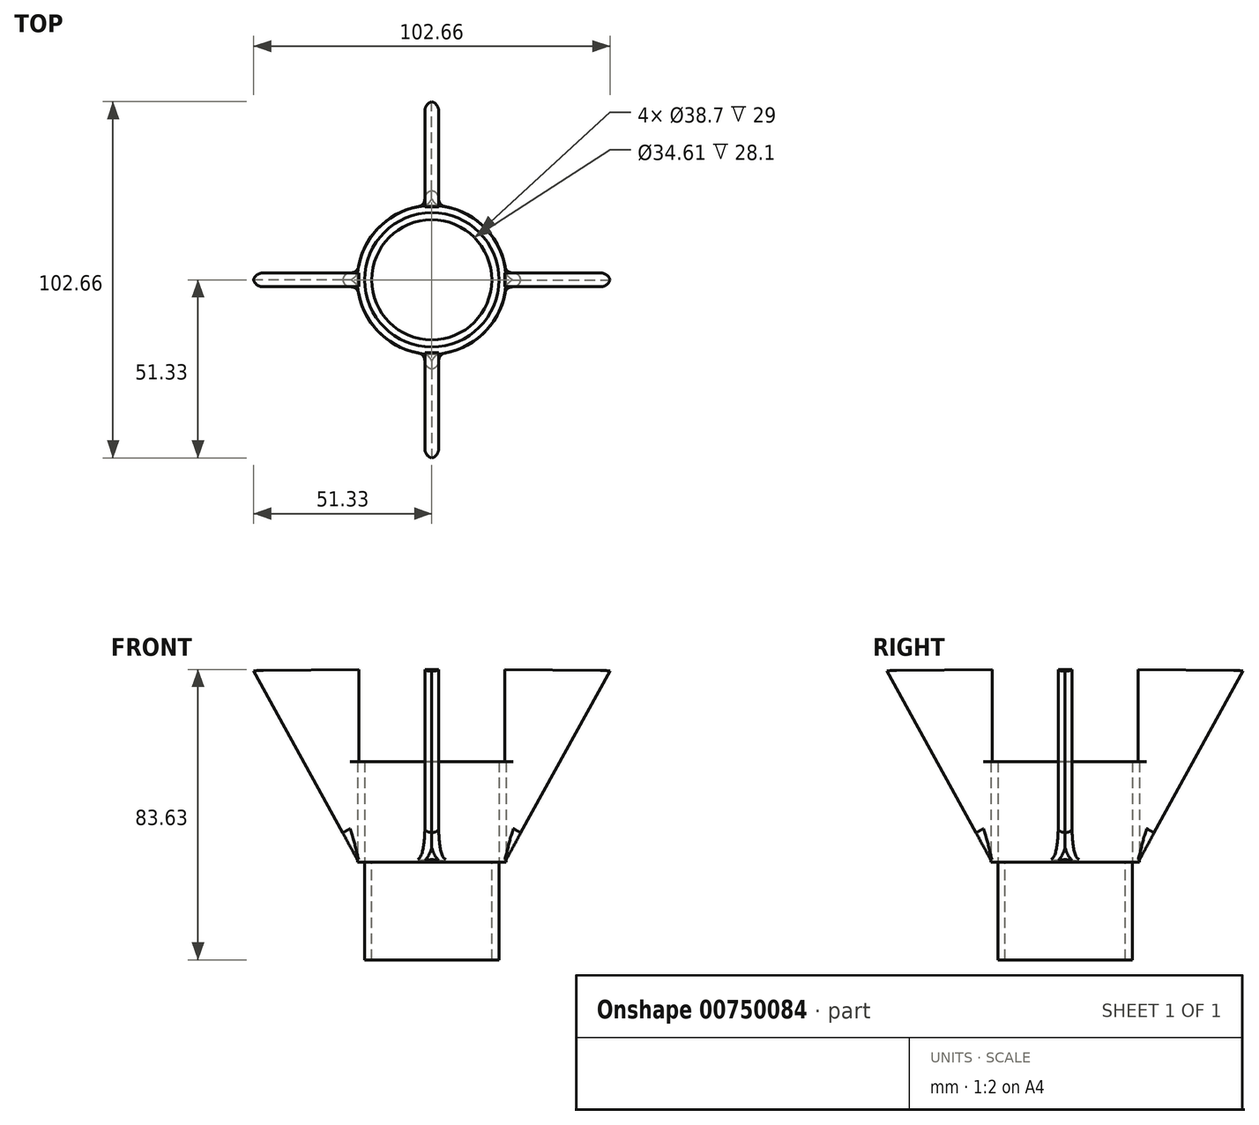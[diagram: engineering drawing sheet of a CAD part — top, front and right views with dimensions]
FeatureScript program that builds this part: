
annotation { "Feature Type Name" : "Feature", "Feature Type Description" : "" }
export const myFeature = defineFeature(function(context is Context, id is Id, definition is map)
    precondition{}
    {
        {
            var Q0;
            Q0=qCreatedBy(makeId("Top.planeOp"),FACE);
            var sketch = newSketch(context, id + "F0", { "sketchPlane" : qUnion([Q0])});
            skCircle(sketch, "E0", {"center": v(0, 0) * mm, "radius": 21.43 * mm});
            skCircle(sketch, "E1", {"center": v(0, 0) * mm, "radius": 19.35 * mm});
            skSolve(sketch);
        }
        {
            var Q0;
            Q0=makeQuery(id+"F0.imprint","IMPRINT",FACE,{"disambiguationData":[TD([[makeQuery(id+"F0.imprint","IMPRINT",EDGE,{"derivedFrom":sQuery(id+"F0.wireOp",EDGE,"E0")}),1.0]])]});
            extrude(context, id + "F1", {"entities" : qUnion([Q0]), "depth" : 29 * mm, "offsetDistance" : 25 * mm});
        }
        {
            var Q0;
            Q0=qCreatedBy(makeId("Top.planeOp"),FACE);
            var sketch = newSketch(context, id + "F2", { "sketchPlane" : qUnion([Q0])});
            skCircle(sketch, "E2", {"center": v(0, 0) * mm, "radius": 19.35 * mm});
            skCircle(sketch, "E3", {"center": v(0, 0) * mm, "radius": 17.3 * mm});
            skSolve(sketch);
        }
        {
            var Q0;
            Q0=makeQuery(id+"F2.imprint","IMPRINT",FACE,{"disambiguationData":[TD([[makeQuery(id+"F2.imprint","IMPRINT",EDGE,{"derivedFrom":sQuery(id+"F2.wireOp",EDGE,"E2")}),1.0]])]});
            extrude(context, id + "F3", {"entities" : qUnion([Q0]), "oppositeDirection" : true, "depth" : 28.1 * mm, "offsetDistance" : 25 * mm});
        }
        {
            var Q0;
            Q0=qCreatedBy(makeId("Front.planeOp"),FACE);
            var sketch = newSketch(context, id + "F4", { "sketchPlane" : qUnion([Q0])});
            skLineSegment(sketch, "E4", {"start": v(-21.02, 0) * mm, "end": v(-51.39, 55.22) * mm});
            skLineSegment(sketch, "E5", {"start": v(-21.02, 0) * mm, "end": v(-21.02, 55.53) * mm});
            skLineSegment(sketch, "E6", {"start": v(-21.02, 55.53) * mm, "end": v(-51.39, 55.22) * mm});
            skSolve(sketch);
        }
        {
            var Q0;
            Q0=makeQuery(id+"F4.imprint","IMPRINT",FACE,{"disambiguationData":[TD([[makeQuery(id+"F4.imprint","IMPRINT",EDGE,{"derivedFrom":sQuery(id+"F4.wireOp",EDGE,"E4")}),-1.0]])]});
            extrude(context, id + "F5", {"entities" : qUnion([Q0]), "operationType" : NewBodyOperationType.ADD, "depth" : 2 * mm, "offsetDistance" : 25 * mm, "hasSecondDirection" : true, "secondDirectionOppositeDirection" : true, "secondDirectionDepth" : 2 * mm});
        }
        {
            var Q0;
            Q0=makeQuery(id+"F5.boolean.opBoolean","INTERSECT",EDGE,{"derivedFrom":[makeQuery(id+"F1.opExtrude","SWEPT_FACE",FACE,{"disambiguationData":[OSD([sQuery(id+"F0.wireOp",EDGE,"E0")])]}),makeQuery(id+"F5.opExtrude","CAP_FACE",FACE,{"disambiguationData":[OSD([sQuery(id+"F4.wireOp",EDGE,"E4"),sQuery(id+"F4.wireOp",EDGE,"E5"),sQuery(id+"F4.wireOp",EDGE,"E6")])],"isStart":false})]});
            var Q1;
            Q1=makeQuery(id+"F5.boolean.opBoolean","INTERSECT",EDGE,{"derivedFrom":[makeQuery(id+"F1.opExtrude","SWEPT_FACE",FACE,{"disambiguationData":[OSD([sQuery(id+"F0.wireOp",EDGE,"E0")])]}),makeQuery(id+"F5.opExtrude","CAP_FACE",FACE,{"disambiguationData":[OSD([sQuery(id+"F4.wireOp",EDGE,"E4"),sQuery(id+"F4.wireOp",EDGE,"E5"),sQuery(id+"F4.wireOp",EDGE,"E6")])],"isStart":true})]});
            var Q2;
            Q2=makeQuery(id+"F9.opPattern","COPY",EDGE,{"derivedFrom":makeQuery(id+"F5.boolean.opBoolean","INTERSECT",EDGE,{"derivedFrom":[makeQuery(id+"F1.opExtrude","SWEPT_FACE",FACE,{"disambiguationData":[OSD([sQuery(id+"F0.wireOp",EDGE,"E0")])]}),makeQuery(id+"F5.opExtrude","CAP_FACE",FACE,{"disambiguationData":[OSD([sQuery(id+"F4.wireOp",EDGE,"E4"),sQuery(id+"F4.wireOp",EDGE,"E5"),sQuery(id+"F4.wireOp",EDGE,"E6")])],"isStart":false})]}),"instanceName":"3"});
            var Q3;
            Q3=makeQuery(id+"F9.opPattern","COPY",EDGE,{"derivedFrom":makeQuery(id+"F5.boolean.opBoolean","INTERSECT",EDGE,{"derivedFrom":[makeQuery(id+"F1.opExtrude","SWEPT_FACE",FACE,{"disambiguationData":[OSD([sQuery(id+"F0.wireOp",EDGE,"E0")])]}),makeQuery(id+"F5.opExtrude","CAP_FACE",FACE,{"disambiguationData":[OSD([sQuery(id+"F4.wireOp",EDGE,"E4"),sQuery(id+"F4.wireOp",EDGE,"E5"),sQuery(id+"F4.wireOp",EDGE,"E6")])],"isStart":true})]}),"instanceName":"3"});
            var Q4;
            Q4=makeQuery(id+"F9.opPattern","COPY",EDGE,{"derivedFrom":makeQuery(id+"F5.boolean.opBoolean","INTERSECT",EDGE,{"derivedFrom":[makeQuery(id+"F1.opExtrude","SWEPT_FACE",FACE,{"disambiguationData":[OSD([sQuery(id+"F0.wireOp",EDGE,"E0")])]}),makeQuery(id+"F5.opExtrude","CAP_FACE",FACE,{"disambiguationData":[OSD([sQuery(id+"F4.wireOp",EDGE,"E4"),sQuery(id+"F4.wireOp",EDGE,"E5"),sQuery(id+"F4.wireOp",EDGE,"E6")])],"isStart":false})]}),"instanceName":"1"});
            var Q5;
            Q5=makeQuery(id+"F9.opPattern","COPY",EDGE,{"derivedFrom":makeQuery(id+"F5.boolean.opBoolean","INTERSECT",EDGE,{"derivedFrom":[makeQuery(id+"F1.opExtrude","SWEPT_FACE",FACE,{"disambiguationData":[OSD([sQuery(id+"F0.wireOp",EDGE,"E0")])]}),makeQuery(id+"F5.opExtrude","CAP_FACE",FACE,{"disambiguationData":[OSD([sQuery(id+"F4.wireOp",EDGE,"E4"),sQuery(id+"F4.wireOp",EDGE,"E5"),sQuery(id+"F4.wireOp",EDGE,"E6")])],"isStart":true})]}),"instanceName":"1"});
            var Q6;
            Q6=makeQuery(id+"F9.opPattern","COPY",EDGE,{"derivedFrom":makeQuery(id+"F5.boolean.opBoolean","INTERSECT",EDGE,{"derivedFrom":[makeQuery(id+"F1.opExtrude","SWEPT_FACE",FACE,{"disambiguationData":[OSD([sQuery(id+"F0.wireOp",EDGE,"E0")])]}),makeQuery(id+"F5.opExtrude","CAP_FACE",FACE,{"disambiguationData":[OSD([sQuery(id+"F4.wireOp",EDGE,"E4"),sQuery(id+"F4.wireOp",EDGE,"E5"),sQuery(id+"F4.wireOp",EDGE,"E6")])],"isStart":false})]}),"instanceName":"2"});
            var Q7;
            Q7=makeQuery(id+"F9.opPattern","COPY",EDGE,{"derivedFrom":makeQuery(id+"F5.boolean.opBoolean","INTERSECT",EDGE,{"derivedFrom":[makeQuery(id+"F1.opExtrude","SWEPT_FACE",FACE,{"disambiguationData":[OSD([sQuery(id+"F0.wireOp",EDGE,"E0")])]}),makeQuery(id+"F5.opExtrude","CAP_FACE",FACE,{"disambiguationData":[OSD([sQuery(id+"F4.wireOp",EDGE,"E4"),sQuery(id+"F4.wireOp",EDGE,"E5"),sQuery(id+"F4.wireOp",EDGE,"E6")])],"isStart":true})]}),"instanceName":"2"});
            fillet(context, id + "F6", {"entities" : qUnion([Q0, Q1, Q2, Q3, Q4, Q5, Q6, Q7]), "radius" : 2.5 * mm, "tangentPropagation" : true, "rho" : 0.5, "crossSection" : FilletCrossSection.CONIC, "allowEdgeOverflow" : false});
        }
        {
            var Q0;
            Q0=qCreatedBy(makeId("Front.planeOp"),FACE);
            var sketch = newSketch(context, id + "F7", { "sketchPlane" : qUnion([Q0])});
            skLineSegment(sketch, "E7", {"start": v(0, 0) * mm, "end": v(0, 28.01) * mm});
            skSolve(sketch);
        }
        {
            var Q0;
            Q0=makeQuery(id+"F9.opPattern","COPY",EDGE,{"derivedFrom":makeQuery(id+"F5.opExtrude","CAP_EDGE",EDGE,{"disambiguationData":[OSD([sQuery(id+"F4.wireOp",EDGE,"E4")])],"isStart":false}),"instanceName":"2"});
            var Q1;
            Q1=makeQuery(id+"F9.opPattern","COPY",EDGE,{"derivedFrom":makeQuery(id+"F5.opExtrude","CAP_EDGE",EDGE,{"disambiguationData":[OSD([sQuery(id+"F4.wireOp",EDGE,"E4")])],"isStart":true}),"instanceName":"2"});
            var Q2;
            Q2=makeQuery(id+"F9.opPattern","COPY",EDGE,{"derivedFrom":makeQuery(id+"F5.opExtrude","CAP_EDGE",EDGE,{"disambiguationData":[OSD([sQuery(id+"F4.wireOp",EDGE,"E4")])],"isStart":true}),"instanceName":"1"});
            var Q3;
            Q3=makeQuery(id+"F9.opPattern","COPY",EDGE,{"derivedFrom":makeQuery(id+"F5.opExtrude","CAP_EDGE",EDGE,{"disambiguationData":[OSD([sQuery(id+"F4.wireOp",EDGE,"E4")])],"isStart":false}),"instanceName":"1"});
            var Q4;
            Q4=makeQuery(id+"F5.opExtrude","CAP_EDGE",EDGE,{"disambiguationData":[OSD([sQuery(id+"F4.wireOp",EDGE,"E4")])],"isStart":false});
            var Q5;
            Q5=makeQuery(id+"F5.opExtrude","CAP_EDGE",EDGE,{"disambiguationData":[OSD([sQuery(id+"F4.wireOp",EDGE,"E4")])],"isStart":true});
            var Q6;
            Q6=makeQuery(id+"F9.opPattern","COPY",EDGE,{"derivedFrom":makeQuery(id+"F5.opExtrude","CAP_EDGE",EDGE,{"disambiguationData":[OSD([sQuery(id+"F4.wireOp",EDGE,"E4")])],"isStart":false}),"instanceName":"3"});
            var Q7;
            Q7=makeQuery(id+"F9.opPattern","COPY",EDGE,{"derivedFrom":makeQuery(id+"F5.opExtrude","CAP_EDGE",EDGE,{"disambiguationData":[OSD([sQuery(id+"F4.wireOp",EDGE,"E4")])],"isStart":true}),"instanceName":"3"});
            fillet(context, id + "F8", {"entities" : qUnion([Q0, Q1, Q2, Q3, Q4, Q5, Q6, Q7]), "radius" : 2.5 * mm, "tangentPropagation" : true, "allowEdgeOverflow" : false});
        }
        {
            var Q0;
            Q0=makeQuery(id+"F1.opExtrude","SWEPT_BODY",BODY,{"disambiguationData":[OSD([sQuery(id+"F0.wireOp",EDGE,"E0"),sQuery(id+"F0.wireOp",EDGE,"E1")])]});
            var Q1;
            Q1=sQuery(id+"F7.wireOp",EDGE,"E7");
            circularPattern(context, id + "F9", {"entities" : qUnion([Q0]), "axis" : qUnion([Q1]), "angle" : 360 * degree, "instanceCount" : 4, "equalSpace" : true});
        }
    });
